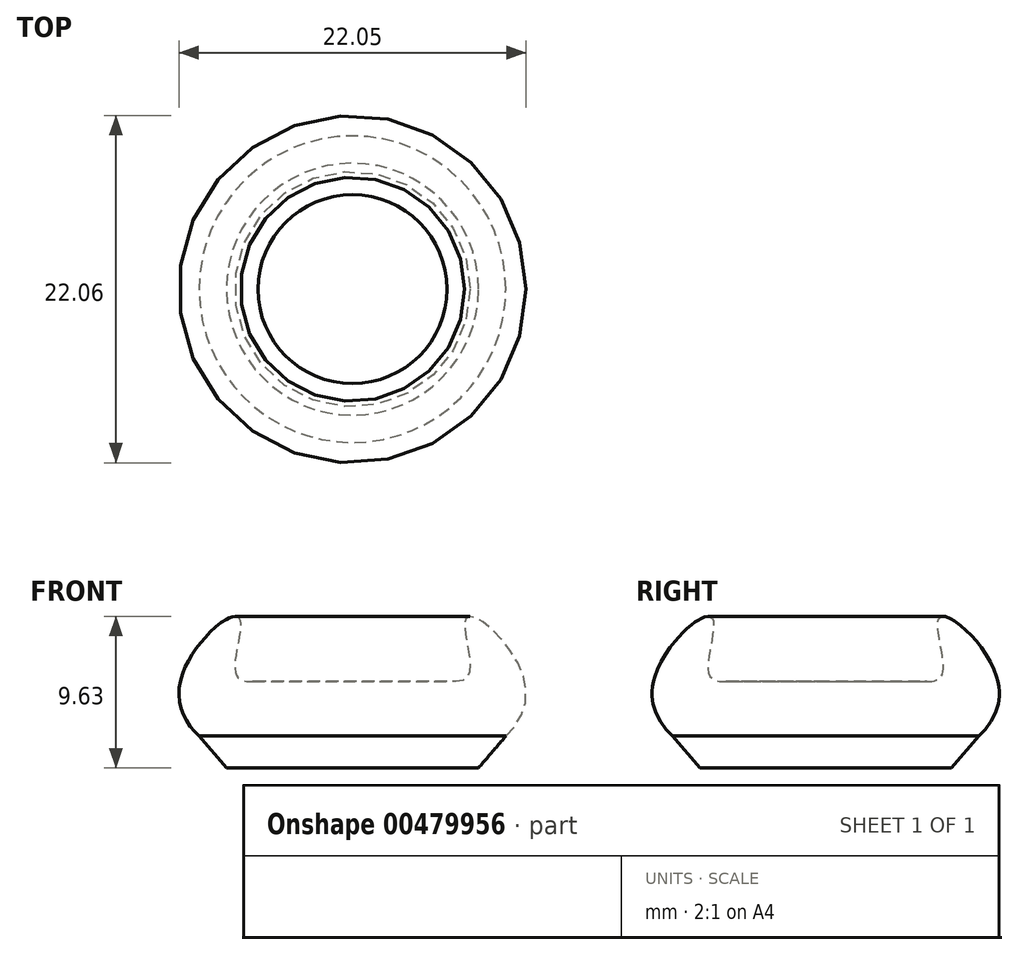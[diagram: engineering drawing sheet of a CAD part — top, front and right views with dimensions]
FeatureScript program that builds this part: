
annotation { "Feature Type Name" : "Feature", "Feature Type Description" : "" }
export const myFeature = defineFeature(function(context is Context, id is Id, definition is map)
    precondition{}
    {
        {
            var Q0;
            Q0=qCreatedBy(makeId("Front.planeOp"),FACE);
            var sketch = newSketch(context, id + "F0", { "sketchPlane" : qUnion([Q0])});
            skFitSpline(sketch, "E0", {"points": [v(-14.62, -20.6) * mm, v(-20.03, -16.31) * mm, v(-16.31, -11.8) * mm, v(-16.5, -15.12) * mm, v(-15.02, -15.9) * mm, v(-9.02, -15.9) * mm, v(-14.62, -20.6) * mm]});
            skLineSegment(sketch, "E1.top", {"start": v(-17.02, -21.4) * mm, "end": v(-9.02, -21.4) * mm});
            skLineSegment(sketch, "E1.right", {"start": v(-9.02, -15.9) * mm, "end": v(-9.02, -21.4) * mm});
            skLineSegment(sketch, "E2", {"start": v(-18.76, -19.36) * mm, "end": v(-17.02, -21.4) * mm});
            skLineSegment(sketch, "E3", {"start": v(-23.49, 0) * mm, "end": v(-2.94, 0) * mm, "construction": true});
            skLineSegment(sketch, "E4", {"start": v(-9.02, -15.9) * mm, "end": v(-15.02, -15.9) * mm});
            skLineSegment(sketch, "E5", {"start": v(-15.02, -15.9) * mm, "end": v(-15.02, -13.19) * mm, "construction": true});
            skSolve(sketch);
        }
        {
            var Q0;
            {var subQ0=sQuery(id+"F0.wireOp",EDGE,"E0");var subQ1=makeQuery(id+"F0.imprint","INTERSECT",VERTEX,{"derivedFrom":[subQ0,sQuery(id+"F0.wireOp",EDGE,"E2")]});Q0=makeQuery(id+"F0.imprint","IMPRINT",FACE,{"disambiguationData":[TD([[makeQuery(id+"F0.imprint","IMPRINT",EDGE,{"disambiguationData":[TD([[subQ1,-1.0]])],"derivedFrom":subQ0}),-1.0]])]});}
            var Q1;
            {var subQ4=sQuery(id+"F0.wireOp",EDGE,"E1.top");Q1=makeQuery(id+"F0.imprint","IMPRINT",FACE,{"disambiguationData":[TD([[makeQuery(id+"F0.imprint","IMPRINT",EDGE,{"derivedFrom":subQ4}),1.0]])]});}
            var Q2;
            Q2=sQuery(id+"F0.wireOp",EDGE,"E1.right");
            revolve(context, id + "F1", {"entities" : qUnion([Q0, Q1]), "axis" : qUnion([Q2]), "revolveType" : RevolveType.FULL});
        }
    });
